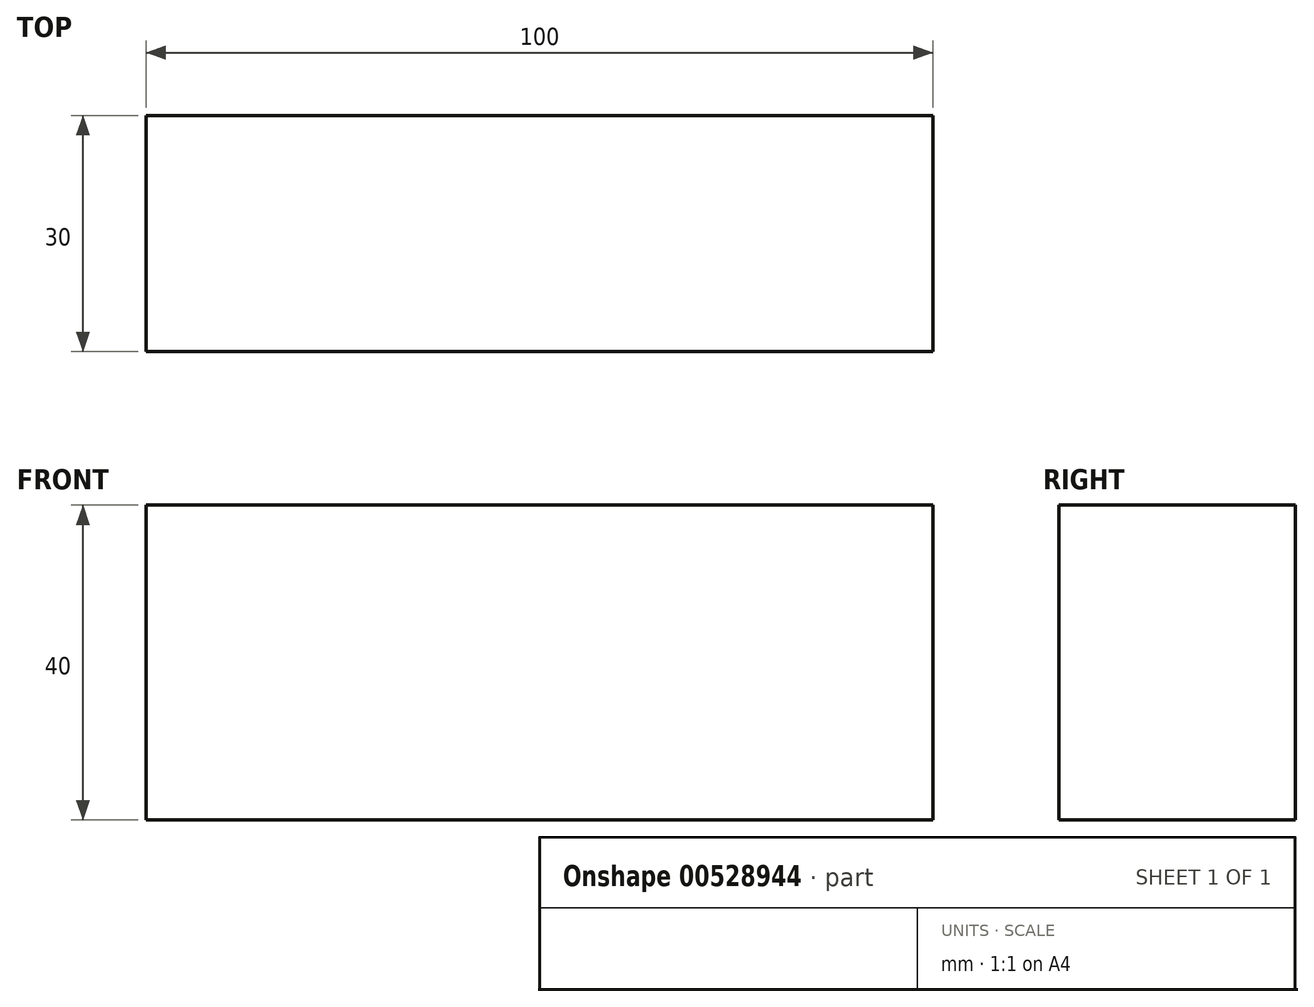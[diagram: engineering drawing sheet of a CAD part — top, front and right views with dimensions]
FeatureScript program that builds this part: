
annotation { "Feature Type Name" : "Feature", "Feature Type Description" : "" }
export const myFeature = defineFeature(function(context is Context, id is Id, definition is map)
    precondition{}
    {
        {
            var Q0;
            Q0=qCreatedBy(makeId("Top.planeOp"),FACE);
            var sketch = newSketch(context, id + "F0", { "sketchPlane" : qUnion([Q0])});
            skLineSegment(sketch, "E0.bottom", {"start": v(50, -15) * mm, "end": v(-50, -15) * mm});
            skLineSegment(sketch, "E0.top", {"start": v(50, 15) * mm, "end": v(-50, 15) * mm});
            skLineSegment(sketch, "E0.left", {"start": v(50, -15) * mm, "end": v(50, 15) * mm});
            skLineSegment(sketch, "E0.right", {"start": v(-50, -15) * mm, "end": v(-50, 15) * mm});
            skPoint(sketch, "E0.middle", {"position": v(0, 0) * mm});
            skSolve(sketch);
        }
        {
            var Q0;
            Q0 = qSketchRegion(id + "F0", true);
            extrude(context, id + "F1", {"entities" : qUnion([Q0]), "depth" : 40 * mm, "offsetDistance" : 25 * mm});
        }
    });
